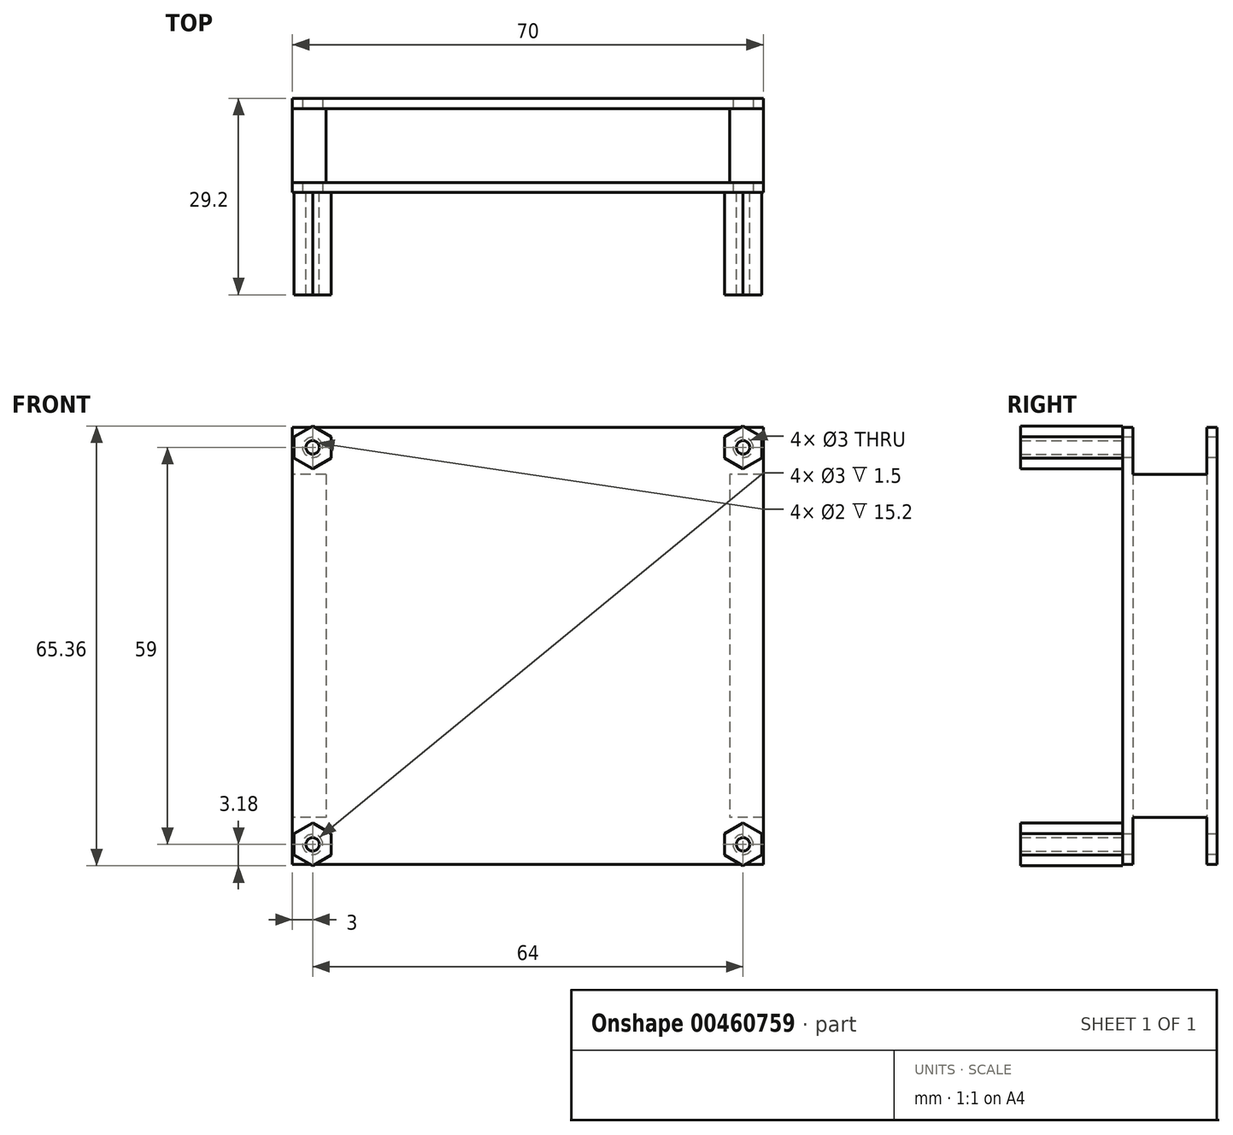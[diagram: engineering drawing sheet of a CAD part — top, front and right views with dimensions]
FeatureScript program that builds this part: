
annotation { "Feature Type Name" : "Feature", "Feature Type Description" : "" }
export const myFeature = defineFeature(function(context is Context, id is Id, definition is map)
    precondition{}
    {
        {
            var Q0;
            Q0=qCreatedBy(makeId("Front.planeOp"),FACE);
            var sketch = newSketch(context, id + "F0", { "sketchPlane" : qUnion([Q0])});
            skLineSegment(sketch, "E0.bottom", {"start": v(0, 0) * mm, "end": v(70, 0) * mm});
            skLineSegment(sketch, "E0.top", {"start": v(0, 65) * mm, "end": v(70, 65) * mm});
            skLineSegment(sketch, "E0.left", {"start": v(0, 0) * mm, "end": v(0, 65) * mm});
            skLineSegment(sketch, "E0.right", {"start": v(70, 0) * mm, "end": v(70, 65) * mm});
            skSolve(sketch);
        }
        {
            var Q0;
            Q0 = qSketchRegion(id + "F0", true);
            extrude(context, id + "F1", {"entities" : qUnion([Q0]), "oppositeDirection" : true, "depth" : 1.5 * mm});
        }
        {
            var Q0;
            Q0=makeQuery(id+"F1.opExtrude","CAP_FACE",FACE,{"disambiguationData":[OSD([sQuery(id+"F0.wireOp",EDGE,"E0.bottom"),sQuery(id+"F0.wireOp",EDGE,"E0.top"),sQuery(id+"F0.wireOp",EDGE,"E0.left"),sQuery(id+"F0.wireOp",EDGE,"E0.right")])],"isStart":false});
            var sketch = newSketch(context, id + "F2", { "sketchPlane" : qUnion([Q0])});
            skLineSegment(sketch, "E1.bottom", {"start": v(-70, 58) * mm, "end": v(-65, 58) * mm});
            skLineSegment(sketch, "E1.top", {"start": v(-70, 7) * mm, "end": v(-65, 7) * mm});
            skLineSegment(sketch, "E1.left", {"start": v(-70, 58) * mm, "end": v(-70, 7) * mm});
            skLineSegment(sketch, "E1.right", {"start": v(-65, 58) * mm, "end": v(-65, 7) * mm});
            skLineSegment(sketch, "E2.bottom", {"start": v(-5, 58) * mm, "end": v(0, 58) * mm});
            skLineSegment(sketch, "E2.top", {"start": v(-5, 7) * mm, "end": v(0, 7) * mm});
            skLineSegment(sketch, "E2.left", {"start": v(-5, 58) * mm, "end": v(-5, 7) * mm});
            skLineSegment(sketch, "E2.right", {"start": v(0, 58) * mm, "end": v(0, 7) * mm});
            skSolve(sketch);
        }
        {
            var Q0;
            Q0 = qSketchRegion(id + "F2", true);
            extrude(context, id + "F3", {"entities" : qUnion([Q0]), "operationType" : NewBodyOperationType.ADD, "depth" : 11 * mm});
        }
        {
            var Q0;
            Q0=makeQuery(id+"F3.opExtrude","CAP_FACE",FACE,{"disambiguationData":[OSD([sQuery(id+"F2.wireOp",EDGE,"E1.bottom"),sQuery(id+"F2.wireOp",EDGE,"E1.top"),sQuery(id+"F2.wireOp",EDGE,"E1.left"),sQuery(id+"F2.wireOp",EDGE,"E1.right")])],"isStart":false});
            var sketch = newSketch(context, id + "F4", { "sketchPlane" : qUnion([Q0])});
            skLineSegment(sketch, "E3.bottom", {"start": v(0, 0) * mm, "end": v(-70, 0) * mm});
            skLineSegment(sketch, "E3.top", {"start": v(0, 65) * mm, "end": v(-70, 65) * mm});
            skLineSegment(sketch, "E3.left", {"start": v(0, 0) * mm, "end": v(0, 65) * mm});
            skLineSegment(sketch, "E3.right", {"start": v(-70, 0) * mm, "end": v(-70, 65) * mm});
            skSolve(sketch);
        }
        {
            var Q0;
            Q0 = qSketchRegion(id + "F4", true);
            extrude(context, id + "F5", {"entities" : qUnion([Q0]), "operationType" : NewBodyOperationType.ADD, "depth" : 1.5 * mm});
        }
        {
            var Q0;
            Q0=qCreatedBy(makeId("Front.planeOp"),FACE);
            var sketch = newSketch(context, id + "F6", { "sketchPlane" : qUnion([Q0])});
            skCircle(sketch, "E4", {"center": v(3, 62) * mm, "radius": 1.5 * mm});
            skCircle(sketch, "E5", {"center": v(67, 62) * mm, "radius": 1.5 * mm});
            skCircle(sketch, "E6", {"center": v(3, 3) * mm, "radius": 1.5 * mm});
            skCircle(sketch, "E7", {"center": v(67, 3) * mm, "radius": 1.5 * mm});
            skLineSegment(sketch, "E8.bottom", {"start": v(3, 62) * mm, "end": v(67, 62) * mm, "construction": true});
            skLineSegment(sketch, "E8.top", {"start": v(3, 3) * mm, "end": v(67, 3) * mm, "construction": true});
            skLineSegment(sketch, "E8.left", {"start": v(3, 62) * mm, "end": v(3, 3) * mm, "construction": true});
            skLineSegment(sketch, "E8.right", {"start": v(67, 62) * mm, "end": v(67, 3) * mm, "construction": true});
            skSolve(sketch);
        }
        {
            var Q0;
            Q0 = qSketchRegion(id + "F6", true);
            extrude(context, id + "F7", {"entities" : qUnion([Q0]), "operationType" : NewBodyOperationType.REMOVE, "oppositeDirection" : true, "depth" : 25 * mm});
        }
        {
            var Q0;
            Q0=makeQuery(id+"F1.opExtrude","CAP_FACE",FACE,{"disambiguationData":[OSD([sQuery(id+"F0.wireOp",EDGE,"E0.bottom"),sQuery(id+"F0.wireOp",EDGE,"E0.top"),sQuery(id+"F0.wireOp",EDGE,"E0.left"),sQuery(id+"F0.wireOp",EDGE,"E0.right")])],"isStart":true});
            var sketch = newSketch(context, id + "F8", { "sketchPlane" : qUnion([Q0])});
            skCircle(sketch, "E9", {"center": v(3, 62) * mm, "radius": 1 * mm});
            skCircle(sketch, "E10.cCircle", {"center": v(3, 62) * mm, "radius": 2.75 * mm, "construction": true});
            skLineSegment(sketch, "E10.0", {"start": v(5.75, 63.59) * mm, "end": v(5.75, 60.41) * mm});
            skLineSegment(sketch, "E10.1", {"start": v(5.75, 60.41) * mm, "end": v(3, 58.82) * mm});
            skLineSegment(sketch, "E10.2", {"start": v(3, 58.82) * mm, "end": v(0.25, 60.41) * mm});
            skLineSegment(sketch, "E10.3", {"start": v(0.25, 60.41) * mm, "end": v(0.25, 63.59) * mm});
            skLineSegment(sketch, "E10.4", {"start": v(0.25, 63.59) * mm, "end": v(3, 65.18) * mm});
            skLineSegment(sketch, "E10.5", {"start": v(3, 65.18) * mm, "end": v(5.75, 63.59) * mm});
            skPoint(sketch, "E10.0.midPoint", {"position": v(5.75, 62) * mm});
            skCircle(sketch, "E11", {"center": v(3, 3) * mm, "radius": 1 * mm});
            skCircle(sketch, "E12.cCircle", {"center": v(3, 3) * mm, "radius": 2.75 * mm, "construction": true});
            skLineSegment(sketch, "E12.0", {"start": v(5.75, 4.59) * mm, "end": v(5.75, 1.41) * mm});
            skLineSegment(sketch, "E12.1", {"start": v(5.75, 1.41) * mm, "end": v(3, -0.18) * mm});
            skLineSegment(sketch, "E12.2", {"start": v(3, -0.18) * mm, "end": v(0.25, 1.41) * mm});
            skLineSegment(sketch, "E12.3", {"start": v(0.25, 1.41) * mm, "end": v(0.25, 4.59) * mm});
            skLineSegment(sketch, "E12.4", {"start": v(0.25, 4.59) * mm, "end": v(3, 6.18) * mm});
            skLineSegment(sketch, "E12.5", {"start": v(3, 6.18) * mm, "end": v(5.75, 4.59) * mm});
            skPoint(sketch, "E12.0.midPoint", {"position": v(5.75, 3) * mm});
            skCircle(sketch, "E13", {"center": v(67, 62) * mm, "radius": 1 * mm});
            skCircle(sketch, "E14.cCircle", {"center": v(67, 62) * mm, "radius": 2.75 * mm, "construction": true});
            skLineSegment(sketch, "E14.0", {"start": v(69.75, 60.41) * mm, "end": v(67, 58.82) * mm});
            skLineSegment(sketch, "E14.1", {"start": v(67, 58.82) * mm, "end": v(64.25, 60.41) * mm});
            skLineSegment(sketch, "E14.2", {"start": v(64.25, 60.41) * mm, "end": v(64.25, 63.59) * mm});
            skLineSegment(sketch, "E14.3", {"start": v(64.25, 63.59) * mm, "end": v(67, 65.18) * mm});
            skLineSegment(sketch, "E14.4", {"start": v(67, 65.18) * mm, "end": v(69.75, 63.59) * mm});
            skLineSegment(sketch, "E14.5", {"start": v(69.75, 63.59) * mm, "end": v(69.75, 60.41) * mm});
            skPoint(sketch, "E14.0.midPoint", {"position": v(68.37, 59.62) * mm});
            skCircle(sketch, "E15", {"center": v(67, 3) * mm, "radius": 1 * mm});
            skCircle(sketch, "E16.cCircle", {"center": v(67, 3) * mm, "radius": 2.75 * mm, "construction": true});
            skLineSegment(sketch, "E16.0", {"start": v(69.75, 1.41) * mm, "end": v(67, -0.18) * mm});
            skLineSegment(sketch, "E16.1", {"start": v(67, -0.18) * mm, "end": v(64.25, 1.41) * mm});
            skLineSegment(sketch, "E16.2", {"start": v(64.25, 1.41) * mm, "end": v(64.25, 4.59) * mm});
            skLineSegment(sketch, "E16.3", {"start": v(64.25, 4.59) * mm, "end": v(67, 6.18) * mm});
            skLineSegment(sketch, "E16.4", {"start": v(67, 6.18) * mm, "end": v(69.75, 4.59) * mm});
            skLineSegment(sketch, "E16.5", {"start": v(69.75, 4.59) * mm, "end": v(69.75, 1.41) * mm});
            skPoint(sketch, "E16.0.midPoint", {"position": v(68.38, 0.62) * mm});
            skSolve(sketch);
        }
        {
            var Q0;
            Q0 = qSketchRegion(id + "F8", true);
            extrude(context, id + "F9", {"entities" : qUnion([Q0]), "operationType" : NewBodyOperationType.ADD, "depth" : 15.2 * mm});
        }
    });
